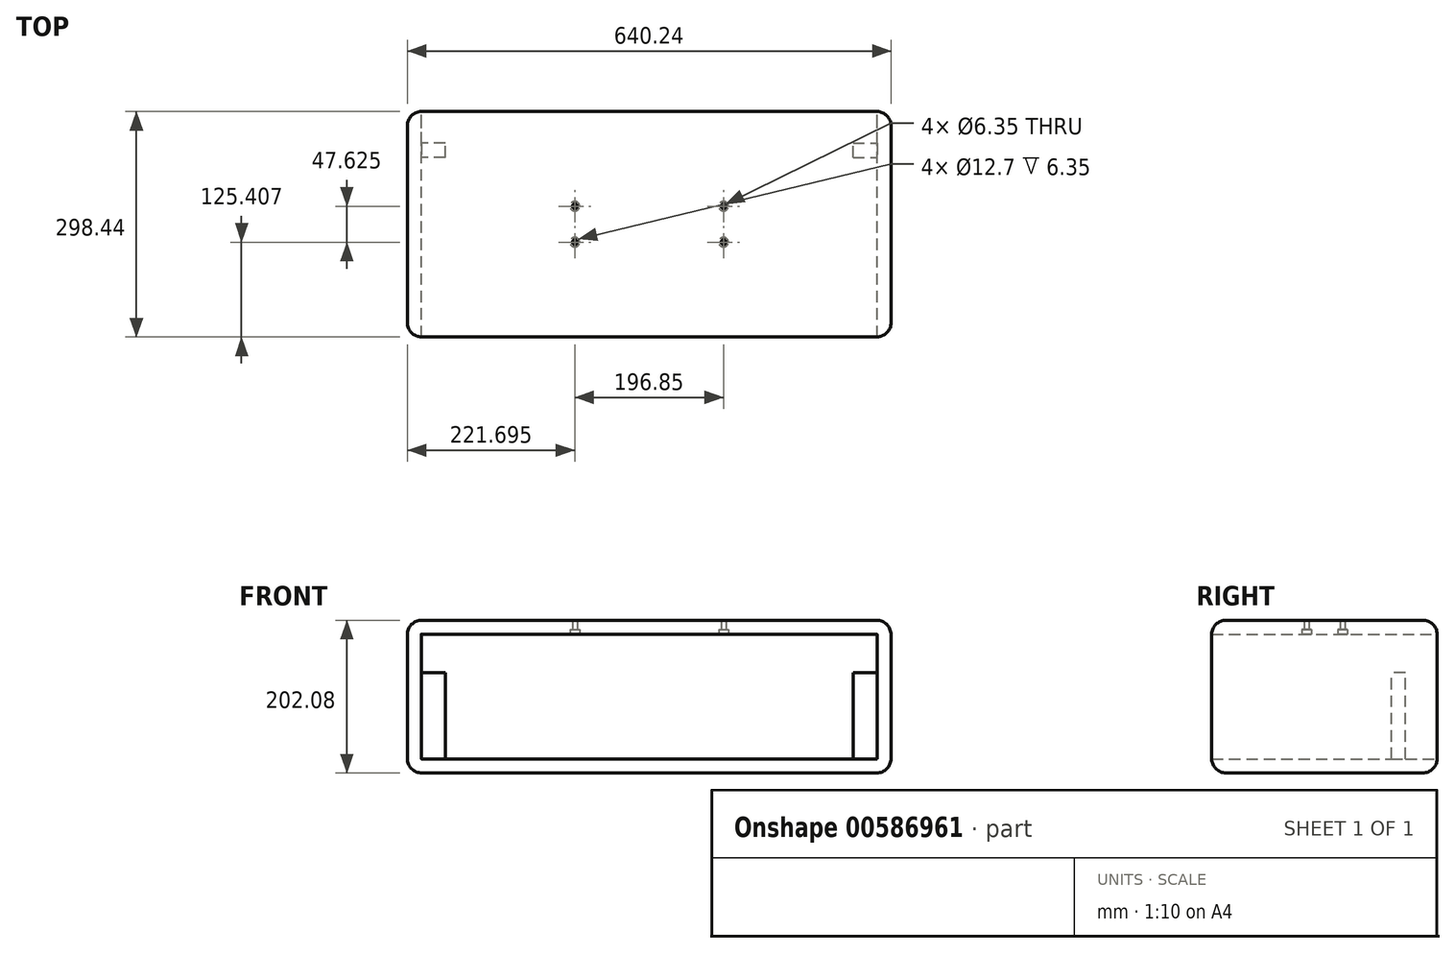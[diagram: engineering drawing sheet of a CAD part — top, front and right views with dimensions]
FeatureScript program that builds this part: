
annotation { "Feature Type Name" : "Feature", "Feature Type Description" : "" }
export const myFeature = defineFeature(function(context is Context, id is Id, definition is map)
    precondition{}
    {
        {
            var Q0;
            Q0=qCreatedBy(makeId("Front.planeOp"),FACE);
            var sketch = newSketch(context, id + "F0", { "sketchPlane" : qUnion([Q0])});
            skLineSegment(sketch, "E0.bottom", {"start": v(320.12, 101.04) * mm, "end": v(-320.12, 101.04) * mm});
            skLineSegment(sketch, "E0.top", {"start": v(320.12, -101.04) * mm, "end": v(-320.12, -101.04) * mm});
            skLineSegment(sketch, "E0.left", {"start": v(320.12, 101.04) * mm, "end": v(320.12, -101.04) * mm});
            skLineSegment(sketch, "E0.right", {"start": v(-320.12, 101.04) * mm, "end": v(-320.12, -101.04) * mm});
            skPoint(sketch, "E0.middle", {"position": v(0, 0) * mm});
            skLineSegment(sketch, "E1.bottom", {"start": v(301.63, 82.55) * mm, "end": v(-301.63, 82.55) * mm});
            skLineSegment(sketch, "E1.top", {"start": v(301.63, -82.55) * mm, "end": v(-301.63, -82.55) * mm});
            skLineSegment(sketch, "E1.left", {"start": v(301.63, 82.55) * mm, "end": v(301.63, -82.55) * mm});
            skLineSegment(sketch, "E1.right", {"start": v(-301.63, 82.55) * mm, "end": v(-301.63, -82.55) * mm});
            skSolve(sketch);
        }
        {
            var Q0;
            Q0=makeQuery(id+"F0.imprint","IMPRINT",FACE,{"disambiguationData":[TD([[makeQuery(id+"F0.imprint","IMPRINT",EDGE,{"derivedFrom":sQuery(id+"F0.wireOp",EDGE,"E0.bottom")}),1.0]])]});
            extrude(context, id + "F1", {"entities" : qUnion([Q0]), "depth" : 149.22 * mm, "offsetDistance" : 25.4 * mm, "hasSecondDirection" : true, "secondDirectionOppositeDirection" : true, "secondDirectionDepth" : 149.22 * mm});
        }
        {
            var Q0;
            Q0=makeQuery(id+"F1.opExtrude","CAP_EDGE",EDGE,{"disambiguationData":[OSD([sQuery(id+"F0.wireOp",EDGE,"E0.bottom")])],"isStart":false});
            var Q1;
            Q1=makeQuery(id+"F1.opExtrude","CAP_EDGE",EDGE,{"disambiguationData":[OSD([sQuery(id+"F0.wireOp",EDGE,"E0.right")])],"isStart":false});
            var Q2;
            Q2=makeQuery(id+"F1.opExtrude","CAP_EDGE",EDGE,{"disambiguationData":[OSD([sQuery(id+"F0.wireOp",EDGE,"E0.top")])],"isStart":false});
            var Q3;
            Q3=makeQuery(id+"F1.opExtrude","CAP_EDGE",EDGE,{"disambiguationData":[OSD([sQuery(id+"F0.wireOp",EDGE,"E0.left")])],"isStart":false});
            fillet(context, id + "F2", {"entities" : qUnion([Q0, Q1, Q2, Q3]), "radius" : 19.05 * mm, "tangentPropagation" : true, "allowEdgeOverflow" : false});
        }
        {
            var Q0;
            Q0=makeQuery(id+"F1.opExtrude","CAP_EDGE",EDGE,{"disambiguationData":[OSD([sQuery(id+"F0.wireOp",EDGE,"E0.left")])],"isStart":true});
            var Q1;
            Q1=makeQuery(id+"F1.opExtrude","CAP_EDGE",EDGE,{"disambiguationData":[OSD([sQuery(id+"F0.wireOp",EDGE,"E0.bottom")])],"isStart":true});
            var Q2;
            Q2=makeQuery(id+"F1.opExtrude","CAP_EDGE",EDGE,{"disambiguationData":[OSD([sQuery(id+"F0.wireOp",EDGE,"E0.top")])],"isStart":true});
            var Q3;
            Q3=makeQuery(id+"F1.opExtrude","CAP_EDGE",EDGE,{"disambiguationData":[OSD([sQuery(id+"F0.wireOp",EDGE,"E0.right")])],"isStart":true});
            fillet(context, id + "F3", {"entities" : qUnion([Q0, Q1, Q2, Q3]), "radius" : 19.05 * mm, "tangentPropagation" : true, "allowEdgeOverflow" : false});
        }
        {
            var Q0;
            Q0=makeQuery(id+"F1.opExtrude","SWEPT_EDGE",EDGE,{"disambiguationData":[OSD([sQuery(id+"F0.wireOp",EDGE,"E0.bottom"),sQuery(id+"F0.wireOp",EDGE,"E0.left")])]});
            var Q1;
            Q1=makeQuery(id+"F1.opExtrude","SWEPT_EDGE",EDGE,{"disambiguationData":[OSD([sQuery(id+"F0.wireOp",EDGE,"E0.top"),sQuery(id+"F0.wireOp",EDGE,"E0.left")])]});
            var Q2;
            Q2=makeQuery(id+"F1.opExtrude","SWEPT_EDGE",EDGE,{"disambiguationData":[OSD([sQuery(id+"F0.wireOp",EDGE,"E0.bottom"),sQuery(id+"F0.wireOp",EDGE,"E0.right")])]});
            var Q3;
            Q3=makeQuery(id+"F1.opExtrude","SWEPT_EDGE",EDGE,{"disambiguationData":[OSD([sQuery(id+"F0.wireOp",EDGE,"E0.top"),sQuery(id+"F0.wireOp",EDGE,"E0.right")])]});
            fillet(context, id + "F4", {"entities" : qUnion([Q0, Q1, Q2, Q3]), "radius" : 19.05 * mm, "tangentPropagation" : true, "allowEdgeOverflow" : false});
        }
        {
            var Q0;
            Q0=makeQuery(id+"F1.opExtrude","SWEPT_FACE",FACE,{"disambiguationData":[OSD([sQuery(id+"F0.wireOp",EDGE,"E1.bottom")])]});
            var sketch = newSketch(context, id + "F5", { "sketchPlane" : qUnion([Q0])});
            skLineSegment(sketch, "E2", {"start": v(0, 0) * mm, "end": v(-301.63, 0) * mm, "construction": true});
            skPoint(sketch, "E3", {"position": v(-98.43, 23.81) * mm});
            skPoint(sketch, "E4", {"position": v(-98.43, -23.81) * mm});
            skLineSegment(sketch, "E5", {"start": v(-98.43, 23.81) * mm, "end": v(-98.43, 0) * mm, "construction": true});
            skLineSegment(sketch, "E6", {"start": v(-98.43, -23.81) * mm, "end": v(-98.43, 0) * mm, "construction": true});
            skLineSegment(sketch, "E7", {"start": v(0, 0) * mm, "end": v(0, 149.22) * mm, "construction": true});
            skLineSegment(sketch, "E8.MirrorCS", {"start": v(98.43, 23.81) * mm, "end": v(98.43, 0) * mm, "construction": true});
            skLineSegment(sketch, "E9.MirrorCS", {"start": v(98.43, -23.81) * mm, "end": v(98.43, 0) * mm, "construction": true});
            skPoint(sketch, "E10.MirrorP", {"position": v(98.43, -23.81) * mm});
            skPoint(sketch, "E11.MirrorP", {"position": v(98.43, 23.81) * mm});
            skSolve(sketch);
        }
        {
            var Q0;
            Q0=sQuery(id+"F5.wireOp",VERTEX,"E3");
            var Q1;
            Q1=sQuery(id+"F5.wireOp",VERTEX,"E4");
            var Q2;
            Q2=sQuery(id+"F5.wireOp",VERTEX,"E11.MirrorP");
            var Q3;
            Q3=sQuery(id+"F5.wireOp",VERTEX,"E10.MirrorP");
            var Q4;
            Q4=makeQuery(id+"F1.opExtrude","SWEPT_BODY",BODY,{"disambiguationData":[OSD([sQuery(id+"F0.wireOp",EDGE,"E0.bottom"),sQuery(id+"F0.wireOp",EDGE,"E0.top"),sQuery(id+"F0.wireOp",EDGE,"E0.left"),sQuery(id+"F0.wireOp",EDGE,"E0.right"),sQuery(id+"F0.wireOp",EDGE,"E1.bottom"),sQuery(id+"F0.wireOp",EDGE,"E1.top"),sQuery(id+"F0.wireOp",EDGE,"E1.left"),sQuery(id+"F0.wireOp",EDGE,"E1.right")])]});
            hole(context, id + "F6", {"style" : HoleStyle.C_BORE, "endStyle" : HoleEndStyle.THROUGH, "holeDiameter" : 6.35 * mm, "cBoreDiameter" : 12.7 * mm, "cBoreDepth" : 6.35 * mm, "majorDiameter" : 6.35 * mm, "isTappedThrough" : true, "tappedDepth" : 12.7 * mm, "tapClearance" : 3, "locations" : qUnion([Q0, Q1, Q2, Q3]), "scope" : qUnion([Q4])});
        }
        {
            var Q0;
            Q0=makeQuery(id+"F1.opExtrude","SWEPT_FACE",FACE,{"disambiguationData":[OSD([sQuery(id+"F0.wireOp",EDGE,"E1.left")])]});
            var sketch = newSketch(context, id + "F7", { "sketchPlane" : qUnion([Q0])});
            skLineSegment(sketch, "E12.bottom", {"start": v(-107.15, -82.55) * mm, "end": v(-88.66, -82.55) * mm});
            skLineSegment(sketch, "E12.top", {"start": v(-107.15, 31.75) * mm, "end": v(-88.66, 31.75) * mm});
            skLineSegment(sketch, "E12.left", {"start": v(-107.15, -82.55) * mm, "end": v(-107.15, 31.75) * mm});
            skLineSegment(sketch, "E12.right", {"start": v(-88.66, -82.55) * mm, "end": v(-88.66, 31.75) * mm});
            skSolve(sketch);
        }
        {
            var Q0;
            Q0=makeQuery(id+"F7.imprint","IMPRINT",FACE,{"disambiguationData":[TD([[makeQuery(id+"F7.imprint","IMPRINT",EDGE,{"derivedFrom":sQuery(id+"F7.wireOp",EDGE,"E12.bottom")}),-1.0]])]});
            extrude(context, id + "F8", {"entities" : qUnion([Q0]), "operationType" : NewBodyOperationType.ADD, "depth" : 31.75 * mm, "offsetDistance" : 25.4 * mm});
        }
        {
            var Q0;
            Q0=makeQuery(id+"F1.opExtrude","SWEPT_BODY",BODY,{"disambiguationData":[OSD([sQuery(id+"F0.wireOp",EDGE,"E0.bottom"),sQuery(id+"F0.wireOp",EDGE,"E0.top"),sQuery(id+"F0.wireOp",EDGE,"E0.left"),sQuery(id+"F0.wireOp",EDGE,"E0.right"),sQuery(id+"F0.wireOp",EDGE,"E1.bottom"),sQuery(id+"F0.wireOp",EDGE,"E1.top"),sQuery(id+"F0.wireOp",EDGE,"E1.left"),sQuery(id+"F0.wireOp",EDGE,"E1.right")])]});
            var Q1;
            Q1=qCreatedBy(makeId("Right.planeOp"),FACE);
            mirror(context, id + "F9", {"operationType" : NewBodyOperationType.ADD, "entities" : qUnion([Q0]), "mirrorPlane" : qUnion([Q1])});
        }
        {
            var Q0;
            Q0=makeQuery(id+"F9.opPattern","COPY",FACE,{"derivedFrom":makeQuery(id+"F8.opExtrude","SWEPT_FACE",FACE,{"disambiguationData":[OSD([sQuery(id+"F7.wireOp",EDGE,"E12.right")])]}),"instanceName":"1"});
            cPlane(context, id + "F10", {"entities" : qUnion([Q0]), "cplaneType" : CPlaneType.OFFSET, "offset" : 237.87 * mm, "width" : 152.4 * mm, "height" : 152.4 * mm});
        }
        {
            var Q0;
            Q0=qCreatedBy(id+"F10.planeOp",FACE);
            var sketch = newSketch(context, id + "F11", { "sketchPlane" : qUnion([Q0])});
            skArc(sketch, "E13", {"start": v(-320.12, 82) * mm, "mid": v(-314.54, 95.46) * mm, "end": v(-301.07, 101.04) * mm});
            skLineSegment(sketch, "E14", {"start": v(-301.07, 82.55) * mm, "end": v(-301.07, 82) * mm});
            skLineSegment(sketch, "E15", {"start": v(-301.07, 82) * mm, "end": v(-301.63, 82) * mm});
            skLineSegment(sketch, "E16", {"start": v(-301.07, 101.04) * mm, "end": v(-294.72, 101.04) * mm});
            skLineSegment(sketch, "E17", {"start": v(-320.12, 82) * mm, "end": v(-320.12, 75.64) * mm});
            skLineSegment(sketch, "E18", {"start": v(-320.12, 75.64) * mm, "end": v(-321.13, 75.64) * mm});
            skLineSegment(sketch, "E19", {"start": v(-294.72, 101.04) * mm, "end": v(-294.72, 102.06) * mm});
            skLineSegment(sketch, "E20", {"start": v(-294.72, 102.06) * mm, "end": v(-301.07, 102.06) * mm});
            skLineSegment(sketch, "E21", {"start": v(-321.13, 75.64) * mm, "end": v(-321.13, 82) * mm});
            skArc(sketch, "E22", {"start": v(-321.13, 82) * mm, "mid": v(-315.26, 96.18) * mm, "end": v(-301.07, 102.06) * mm});
            skLineSegment(sketch, "E23", {"start": v(-320.12, 82) * mm, "end": v(-301.63, 82) * mm});
            skLineSegment(sketch, "E24", {"start": v(-301.07, 82.55) * mm, "end": v(-301.07, 101.04) * mm});
            skSolve(sketch);
        }
        {
            var Q0;
            Q0 = qSketchRegion(id + "F11", true);
            extrude(context, id + "F12", {"entities" : qUnion([Q0]), "oppositeDirection" : true, "depth" : 44.2 * mm, "offsetDistance" : 25.4 * mm, "hasSecondDirection" : true, "secondDirectionOppositeDirection" : false, "secondDirectionDepth" : 1.02 * mm});
        }
        {
            var Q0;
            Q0=makeQuery(id+"F12.opExtrude","CAP_EDGE",EDGE,{"disambiguationData":[OSD([sQuery(id+"F11.wireOp",EDGE,"E22")])],"isStart":true});
            fillet(context, id + "F13", {"entities" : qUnion([Q0]), "radius" : 19.05 * mm, "tangentPropagation" : true, "allowEdgeOverflow" : false});
        }
        {
            var Q0;
            Q0=makeQuery(id+"F1.opExtrude","SWEPT_BODY",BODY,{"disambiguationData":[OSD([sQuery(id+"F0.wireOp",EDGE,"E0.bottom"),sQuery(id+"F0.wireOp",EDGE,"E0.top"),sQuery(id+"F0.wireOp",EDGE,"E0.left"),sQuery(id+"F0.wireOp",EDGE,"E0.right"),sQuery(id+"F0.wireOp",EDGE,"E1.bottom"),sQuery(id+"F0.wireOp",EDGE,"E1.top"),sQuery(id+"F0.wireOp",EDGE,"E1.left"),sQuery(id+"F0.wireOp",EDGE,"E1.right")])]});
            var Q1;
            Q1=makeQuery(id+"F12.opExtrude","SWEPT_BODY",BODY,{"disambiguationData":[OSD([sQuery(id+"F11.wireOp",EDGE,"E14"),sQuery(id+"F11.wireOp",EDGE,"E15"),sQuery(id+"F11.wireOp",EDGE,"E16"),sQuery(id+"F11.wireOp",EDGE,"E17"),sQuery(id+"F11.wireOp",EDGE,"E18"),sQuery(id+"F11.wireOp",EDGE,"E19"),sQuery(id+"F11.wireOp",EDGE,"E20"),sQuery(id+"F11.wireOp",EDGE,"E21"),sQuery(id+"F11.wireOp",EDGE,"E22"),sQuery(id+"F11.wireOp",EDGE,"E23"),sQuery(id+"F11.wireOp",EDGE,"E24")])]});
            booleanBodies(context, id + "F14", {"operationType" : BooleanOperationType.SUBTRACTION, "tools" : qUnion([Q0]), "targets" : qUnion([Q1]), "keepTools" : true});
        }
        {
            var Q0;
            Q0=makeQuery(id+"F12.opExtrude","SWEPT_BODY",BODY,{"disambiguationData":[OSD([sQuery(id+"F11.wireOp",EDGE,"E14"),sQuery(id+"F11.wireOp",EDGE,"E15"),sQuery(id+"F11.wireOp",EDGE,"E16"),sQuery(id+"F11.wireOp",EDGE,"E17"),sQuery(id+"F11.wireOp",EDGE,"E18"),sQuery(id+"F11.wireOp",EDGE,"E19"),sQuery(id+"F11.wireOp",EDGE,"E20"),sQuery(id+"F11.wireOp",EDGE,"E21"),sQuery(id+"F11.wireOp",EDGE,"E22"),sQuery(id+"F11.wireOp",EDGE,"E23"),sQuery(id+"F11.wireOp",EDGE,"E24")])]});
            deleteBodies(context, id + "F15", {"entities" : qUnion([Q0])});
        }
    });
